# Revit family: Hager-Type B SP&N Distribution Boards-Surface_mounted-IP2XC-With_Cover-With_DIN-Hosted-GB-en
name_source: partatom
category: Electrical Equipment
units: mm (PartAtom-declared; Revit-internal decimal feet)

## family parameters
Cut with Voids When Loaded = No
Host = Face
Maintain Annotation Orientation = Yes
Panel Configuration = Two Columns, Circuits Across
Part Type = Panelboard
Room Calculation Point = No
Round Connector Dimension = Use Diameter
Shared = No

## types (1)
- Type B SP&N Distribution Boards-Surface_mounted_W465_H300_D165_16_Modular_Spacing-JK216EG
    BC_MODEL_ID = 1554189
    BC_OBJECT_ID = 513816
    BC_OBJECT_VERSION = #1
    BC_VARIANT_ID = 1178536
    Code hager = ADD-EC000214_EU
    Default Elevation = 0 mm  [stored 0 ft]
    EF000003 - Mounting method = Surface mounted
    EF000008 - Width = 465 mm  [stored 1.52559 ft]
    EF000024 - UV resistant = No
    EF000040 - Height = 300 mm  [stored 0.984252 ft]
    EF000049 - Depth = 165 mm  [stored 0.541339 ft]
    EF000116 - RAL number = 7035
    EF000118 - With mounting plate = No
    EF000218 - Recess depth = 0 mm  [stored 0 ft]
    EF000266 - Number of rows = 1
    EF000332 - Recess height = 0 mm  [stored 0 ft]
    EF000846 - Recess width = 0 mm  [stored 0 ft]
    EF001062 - EMC-version = No
    EF001088 - Extension possible = No
    EF001131 - Internal depth = 0 mm  [stored 0 ft]
    EF001134 - With DIN-rail = Yes
    EF002950 - Width in number of modular spacings = 16
    EF005474 - Degree of protection (IP rating) = IP2XC
    EF006244 - Transparent cover/door = No
    EF006306 - With lock = No
    EF015776 - Earthing terminal block = Yes
    EF015777 - Neutral terminal block = Yes
    EF015941 - Signal passing door = No
    ETIM class code = EC000214
    ETIM class name = Small distribution board
    HG000001-Number of columns = 1
    HG000002-With door or cover = Yes
    HG000003-Range = Type B SP&N Distribution Boards
    HG000004-Manufacturer reference = JK216EG
    HG000005-Thickness = 2 mm  [stored 0.00656168 ft]
    HG000006-Flush mounted = No
    HG000007-Number of empty columns = 0
    HG000008-Number of empty rows = 0
    HG000009-Double swing door = No
    HG000010-Asymmetric doors = No
    HG000011-Empty rows from bottom = No
    HG000012-Door swing angle = 90.00°
    HG000013-Door on the left = No
    HG000014-Door on the right = Yes
    HG000015-Clearance visibility = Yes
    HG000016-Door 3D visibility = Yes
    HG000017-Distance between poles = 18 mm  [stored 0.0590551 ft]
    HG000060-RAL-number = 7035
    HG000099-Onfly Template ID = 507532
    HGEF000266-Number of rows = 1
    HGEF002950-Width in number of modular spacings = 16
    Manufacturer = Hager
    Name = Type B SP&N Distribution Boards-Surface_mounted-IP2XC-With_Cover-With_DIN-GB
    Name BIM&CO = Electricity
    Name hager = ADD_Enclosures_EC000214
    Reference = Type B SP&N Distribution Boards-Surface_mounted_W465_H300_D165_16_Modular_Spacing-JK216EG
    Uniformat = Low Tension Service & Dist.
    Uniformat code = D501001

note: [stored X ft] marks values corroborated as IEEE doubles in the binary element streams (Revit-internal decimal feet)

## geometry (parser evidence)
native form markers: Sweep x14
no freeform markers — native parametric forms only
